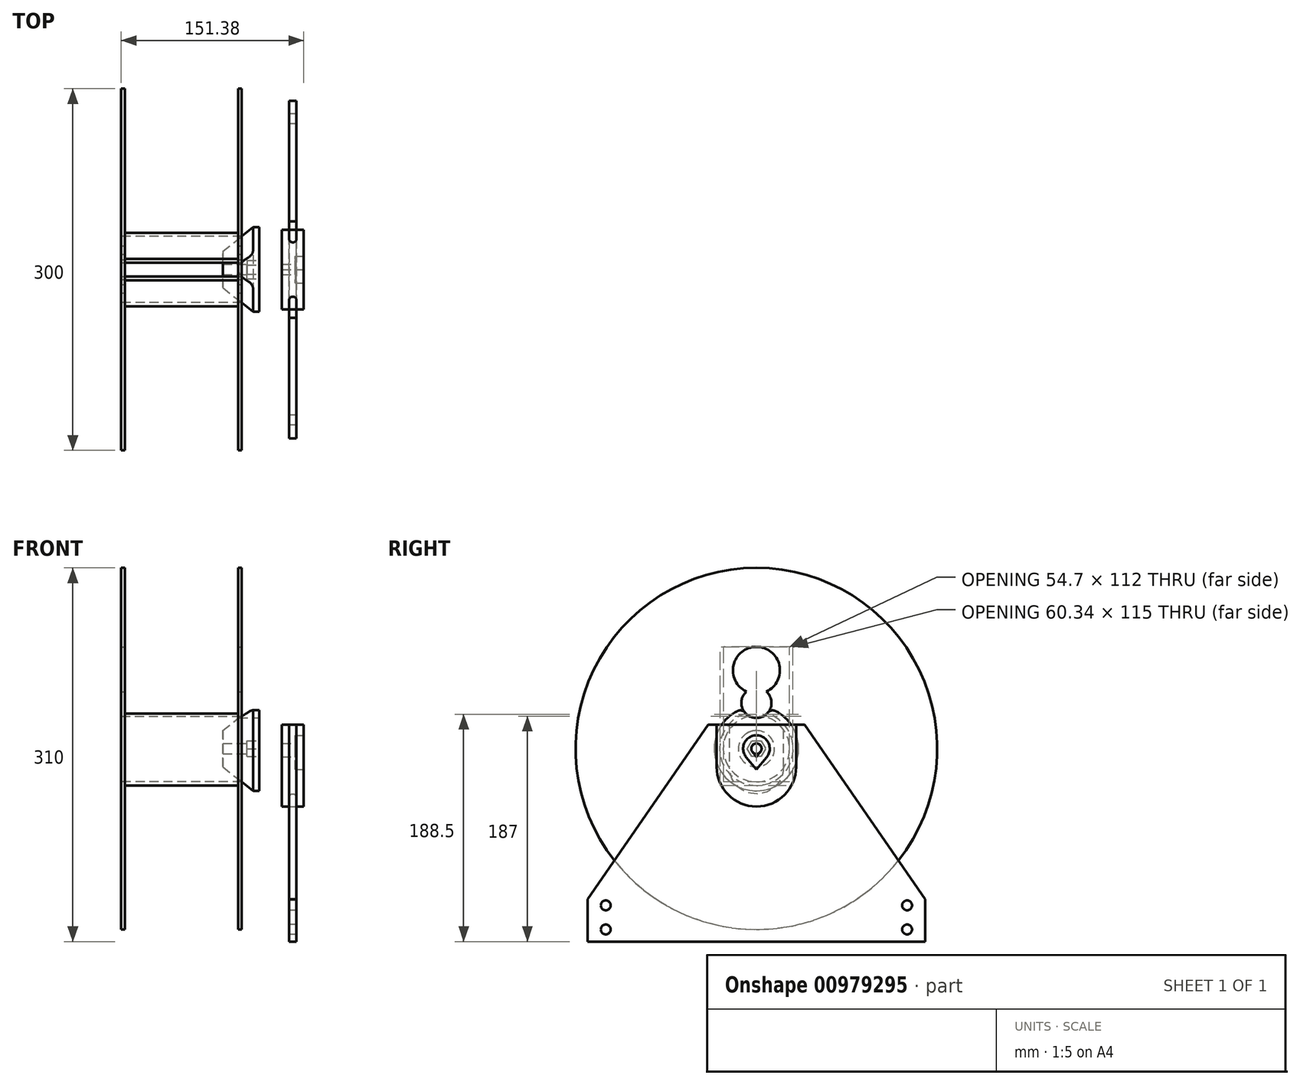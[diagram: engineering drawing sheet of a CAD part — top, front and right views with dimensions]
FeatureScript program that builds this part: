
annotation { "Feature Type Name" : "Feature", "Feature Type Description" : "" }
export const myFeature = defineFeature(function(context is Context, id is Id, definition is map)
    precondition{}
    {
        {
            var Q0;
            Q0=qCreatedBy(makeId("Front.planeOp"),FACE);
            var sketch = newSketch(context, id + "F0", { "sketchPlane" : qUnion([Q0])});
            skLineSegment(sketch, "E0", {"start": v(-50, 150) * mm, "end": v(-50, 27.5) * mm});
            skLineSegment(sketch, "E1", {"start": v(-50, 27.5) * mm, "end": v(50, 27.5) * mm});
            skLineSegment(sketch, "E2", {"start": v(50, 27.5) * mm, "end": v(50, 150) * mm});
            skLineSegment(sketch, "E3", {"start": v(50, 150) * mm, "end": v(47, 150) * mm});
            skLineSegment(sketch, "E4", {"start": v(47, 150) * mm, "end": v(47, 30.5) * mm});
            skLineSegment(sketch, "E5", {"start": v(47, 30.5) * mm, "end": v(-47, 30.5) * mm});
            skLineSegment(sketch, "E6", {"start": v(-47, 30.5) * mm, "end": v(-47, 150) * mm});
            skLineSegment(sketch, "E7", {"start": v(-47, 150) * mm, "end": v(-50, 150) * mm});
            skLineSegment(sketch, "E8", {"start": v(-95.65, 0) * mm, "end": v(81.07, 0) * mm, "construction": true});
            skLineSegment(sketch, "E9", {"start": v(0, 27.5) * mm, "end": v(0, 0) * mm, "construction": true});
            skSolve(sketch);
        }
        {
            var Q0;
            Q0=makeQuery(id+"F0.imprint","IMPRINT",FACE,{"disambiguationData":[TD([[makeQuery(id+"F0.imprint","IMPRINT",EDGE,{"derivedFrom":sQuery(id+"F0.wireOp",EDGE,"E0")}),1.0]])]});
            var Q1;
            Q1=sQuery(id+"F0.wireOp",EDGE,"E8");
            revolve(context, id + "F1", {"surfaceOperationType" : NewSurfaceOperationType.NEW, "entities" : qUnion([Q0]), "axis" : qUnion([Q1]), "revolveType" : RevolveType.FULL});
        }
        {
            var Q0;
            Q0=makeQuery(id+"F1.opRevolve","SWEPT_FACE",FACE,{"disambiguationData":[OSD([sQuery(id+"F0.wireOp",EDGE,"E2")])]});
            var sketch = newSketch(context, id + "F2", { "sketchPlane" : qUnion([Q0])});
            skCircle(sketch, "E10", {"center": v(0, 65) * mm, "radius": 19.5 * mm});
            skSolve(sketch);
        }
        {
            var Q0;
            Q0=makeQuery(id+"F2.imprint","IMPRINT",FACE,{"disambiguationData":[TD([[makeQuery(id+"F2.imprint","IMPRINT",EDGE,{"derivedFrom":sQuery(id+"F2.wireOp",EDGE,"E10")}),1.0]])]});
            extrude(context, id + "F3", {"entities" : qUnion([Q0]), "operationType" : NewBodyOperationType.REMOVE, "endBound" : BoundingType.THROUGH_ALL, "oppositeDirection" : true, "depth" : 25 * mm, "offsetDistance" : 25 * mm});
        }
        {
            var Q0;
            Q0=qCreatedBy(makeId("Front.planeOp"),FACE);
            var sketch = newSketch(context, id + "F4", { "sketchPlane" : qUnion([Q0])});
            skLineSegment(sketch, "E11", {"start": v(12.06, 0) * mm, "end": v(93.62, 0) * mm, "construction": true});
            skLineSegment(sketch, "E12", {"start": v(-35, 27.5) * mm, "end": v(50, 27.5) * mm, "construction": true});
            skLineSegment(sketch, "E13", {"start": v(35, -27.5) * mm, "end": v(-35, -27.5) * mm, "construction": true});
            skLineSegment(sketch, "E14", {"start": v(34.37, 4.1) * mm, "end": v(64.37, 4.1) * mm});
            skLineSegment(sketch, "E15", {"start": v(64.37, 4.1) * mm, "end": v(64.37, 35) * mm});
            skLineSegment(sketch, "E16", {"start": v(64.37, 35) * mm, "end": v(59.37, 35) * mm});
            skLineSegment(sketch, "E17", {"start": v(59.37, 35) * mm, "end": v(34.37, 15) * mm});
            skLineSegment(sketch, "E18", {"start": v(34.37, 15) * mm, "end": v(34.37, 4.1) * mm});
            skSolve(sketch);
        }
        {
            var Q0;
            Q0=qSketchRegion(id+"F4",true);
            var Q1;
            Q1=sQuery(id+"F4.wireOp",EDGE,"E11");
            revolve(context, id + "F5", {"surfaceOperationType" : NewSurfaceOperationType.NEW, "entities" : qUnion([Q0]), "axis" : qUnion([Q1]), "revolveType" : RevolveType.FULL});
        }
        {
            var Q0;
            Q0=makeQuery(id+"F5.opRevolve","SWEPT_FACE",FACE,{"disambiguationData":[OSD([sQuery(id+"F4.wireOp",EDGE,"E15")])]});
            var sketch = newSketch(context, id + "F6", { "sketchPlane" : qUnion([Q0])});
            skCircle(sketch, "E19", {"center": v(0, 38) * mm, "radius": 12.5 * mm});
            skSolve(sketch);
        }
        {
            var Q0;
            Q0=qSketchRegion(id+"F6",true);
            extrude(context, id + "F7", {"entities" : qUnion([Q0]), "operationType" : NewBodyOperationType.REMOVE, "endBound" : BoundingType.THROUGH_ALL, "oppositeDirection" : true, "depth" : 25 * mm, "offsetDistance" : 25 * mm});
        }
        {
            var Q0;
            Q0=makeQuery(id+"F7.boolean.opBoolean","INTERSECT",EDGE,{"disambiguationData":[OD(1.0)],"derivedFrom":[makeQuery(id+"F5.opRevolve","SWEPT_FACE",FACE,{"disambiguationData":[OSD([sQuery(id+"F4.wireOp",EDGE,"E16")])]}),makeQuery(id+"F7.opExtrude","SWEPT_FACE",FACE,{"disambiguationData":[OSD([sQuery(id+"F6.wireOp",EDGE,"E19")])]})]});
            var Q1;
            Q1=makeQuery(id+"F7.boolean.opBoolean","INTERSECT",EDGE,{"disambiguationData":[OD(0.0)],"derivedFrom":[makeQuery(id+"F5.opRevolve","SWEPT_FACE",FACE,{"disambiguationData":[OSD([sQuery(id+"F4.wireOp",EDGE,"E16")])]}),makeQuery(id+"F7.opExtrude","SWEPT_FACE",FACE,{"disambiguationData":[OSD([sQuery(id+"F6.wireOp",EDGE,"E19")])]})]});
            fillet(context, id + "F8", {"entities" : qUnion([Q0, Q1]), "radius" : 5 * mm, "tangentPropagation" : true, "allowEdgeOverflow" : false});
        }
        {
            var Q0;
            Q0=makeQuery(id+"F5.opRevolve","SWEPT_FACE",FACE,{"disambiguationData":[OSD([sQuery(id+"F4.wireOp",EDGE,"E15")])]});
            var sketch = newSketch(context, id + "F9", { "sketchPlane" : qUnion([Q0])});
            skCircle(sketch, "E20.cCircle", {"center": v(0, 0) * mm, "radius": 6.55 * mm, "construction": true});
            skLineSegment(sketch, "E20.0", {"start": v(-3.78, 6.55) * mm, "end": v(3.78, 6.55) * mm});
            skLineSegment(sketch, "E20.1", {"start": v(3.78, 6.55) * mm, "end": v(7.56, 0) * mm});
            skLineSegment(sketch, "E20.2", {"start": v(7.56, 0) * mm, "end": v(3.78, -6.55) * mm});
            skLineSegment(sketch, "E20.3", {"start": v(3.78, -6.55) * mm, "end": v(-3.78, -6.55) * mm});
            skLineSegment(sketch, "E20.4", {"start": v(-3.78, -6.55) * mm, "end": v(-7.56, 0) * mm});
            skLineSegment(sketch, "E20.5", {"start": v(-7.56, 0) * mm, "end": v(-3.78, 6.55) * mm});
            skPoint(sketch, "E20.0.midPoint", {"position": v(0, 6.55) * mm});
            skSolve(sketch);
        }
        {
            var Q0;
            Q0=qSketchRegion(id+"F9",true);
            extrude(context, id + "F10", {"entities" : qUnion([Q0]), "operationType" : NewBodyOperationType.REMOVE, "oppositeDirection" : true, "depth" : 10 * mm, "offsetDistance" : 25 * mm});
        }
        {
            var Q0;
            Q0=makeQuery(id+"F5.opRevolve","SWEPT_BODY",BODY,{"disambiguationData":[OSD([sQuery(id+"F4.wireOp",EDGE,"E14"),sQuery(id+"F4.wireOp",EDGE,"E15"),sQuery(id+"F4.wireOp",EDGE,"E16"),sQuery(id+"F4.wireOp",EDGE,"E17"),sQuery(id+"F4.wireOp",EDGE,"E18")])]});
            transform(context, id + "F11", {"entities" : qUnion([Q0]), "transformType" : TransformType.TRANSLATION_3D, "dx" : 0 * mm, "dy" : 0 * mm, "dz" : 0 * mm, "makeCopy" : true});
        }
        {
            var Q0;
            Q0=makeQuery(id+"F11.opPattern","COPY",BODY,{"derivedFrom":makeQuery(id+"F5.opRevolve","SWEPT_BODY",BODY,{"disambiguationData":[OSD([sQuery(id+"F4.wireOp",EDGE,"E14"),sQuery(id+"F4.wireOp",EDGE,"E15"),sQuery(id+"F4.wireOp",EDGE,"E16"),sQuery(id+"F4.wireOp",EDGE,"E17"),sQuery(id+"F4.wireOp",EDGE,"E18")])]}),"instanceName":"1"});
            deleteBodies(context, id + "F12", {"entities" : qUnion([Q0])});
        }
        {
            var Q0;
            Q0=makeQuery(id+"F5.opRevolve","SWEPT_FACE",FACE,{"disambiguationData":[OSD([sQuery(id+"F4.wireOp",EDGE,"E15")])]});
            cPlane(context, id + "F13", {"entities" : qUnion([Q0]), "cplaneType" : CPlaneType.OFFSET, "offset" : 25 * mm, "width" : 150 * mm, "height" : 150 * mm});
        }
        {
            var Q0;
            Q0=qCreatedBy(id+"F13.planeOp",FACE);
            var sketch = newSketch(context, id + "F14", { "sketchPlane" : qUnion([Q0])});
            skLineSegment(sketch, "E21", {"start": v(-140, -160) * mm, "end": v(-140, -125) * mm});
            skLineSegment(sketch, "E22", {"start": v(-140, -125) * mm, "end": v(-40, 20) * mm});
            skLineSegment(sketch, "E23", {"start": v(-40, 20) * mm, "end": v(-25, 20) * mm});
            skLineSegment(sketch, "E24", {"start": v(-25, 20) * mm, "end": v(-25, -15) * mm});
            skLineSegment(sketch, "E25", {"start": v(-25, -15) * mm, "end": v(25, -15) * mm, "construction": true});
            skLineSegment(sketch, "E26", {"start": v(25, -15) * mm, "end": v(25, 20) * mm});
            skLineSegment(sketch, "E27", {"start": v(25, 20) * mm, "end": v(40, 20) * mm});
            skLineSegment(sketch, "E28", {"start": v(40, 20) * mm, "end": v(140, -125) * mm});
            skLineSegment(sketch, "E29", {"start": v(140, -125) * mm, "end": v(140, -160) * mm});
            skLineSegment(sketch, "E30", {"start": v(140, -160) * mm, "end": v(-140, -160) * mm});
            skLineSegment(sketch, "E31", {"start": v(0, -160) * mm, "end": v(0, 0) * mm, "construction": true});
            skArc(sketch, "E32", {"start": v(-25, -15) * mm, "mid": v(0, -40) * mm, "end": v(25, -15) * mm});
            skCircle(sketch, "E33", {"center": v(-125, -130) * mm, "radius": 4.1 * mm});
            skCircle(sketch, "E34", {"center": v(-125, -150) * mm, "radius": 4.1 * mm});
            skCircle(sketch, "E35", {"center": v(125, -130) * mm, "radius": 4.1 * mm});
            skCircle(sketch, "E36", {"center": v(125, -150) * mm, "radius": 4.1 * mm});
            skLineSegment(sketch, "E37", {"start": v(-125, -130) * mm, "end": v(125, -130) * mm, "construction": true});
            skLineSegment(sketch, "E38", {"start": v(125, -130) * mm, "end": v(125, -150) * mm, "construction": true});
            skLineSegment(sketch, "E39", {"start": v(125, -150) * mm, "end": v(-125, -150) * mm, "construction": true});
            skLineSegment(sketch, "E40", {"start": v(-125, -150) * mm, "end": v(-125, -130) * mm, "construction": true});
            skSolve(sketch);
        }
        {
            var Q0;
            Q0=makeQuery(id+"F14.imprint","IMPRINT",FACE,{"disambiguationData":[TD([[makeQuery(id+"F14.imprint","IMPRINT",EDGE,{"derivedFrom":sQuery(id+"F14.wireOp",EDGE,"E21")}),-1.0]])]});
            extrude(context, id + "F15", {"entities" : qUnion([Q0]), "depth" : 6 * mm, "offsetDistance" : 25 * mm});
        }
        {
            var Q0;
            Q0=makeQuery(id+"F15.opExtrude","CAP_FACE",FACE,{"disambiguationData":[OSD([sQuery(id+"F14.wireOp",EDGE,"E21"),sQuery(id+"F14.wireOp",EDGE,"E22"),sQuery(id+"F14.wireOp",EDGE,"E23"),sQuery(id+"F14.wireOp",EDGE,"E24"),sQuery(id+"F14.wireOp",EDGE,"E26"),sQuery(id+"F14.wireOp",EDGE,"E27"),sQuery(id+"F14.wireOp",EDGE,"E28"),sQuery(id+"F14.wireOp",EDGE,"E29"),sQuery(id+"F14.wireOp",EDGE,"E30"),sQuery(id+"F14.wireOp",EDGE,"E32"),sQuery(id+"F14.wireOp",EDGE,"E33"),sQuery(id+"F14.wireOp",EDGE,"E34"),sQuery(id+"F14.wireOp",EDGE,"E35"),sQuery(id+"F14.wireOp",EDGE,"E36")])],"isStart":false});
            cPlane(context, id + "F16", {"entities" : qUnion([Q0]), "cplaneType" : CPlaneType.OFFSET, "offset" : 3 * mm, "oppositeDirection" : true, "width" : 150 * mm, "height" : 150 * mm});
        }
        {
            var Q0;
            Q0=qCreatedBy(id+"F16.planeOp",FACE);
            var sketch = newSketch(context, id + "F17", { "sketchPlane" : qUnion([Q0])});
            skLineSegment(sketch, "E41.0", {"start": v(-25, 20) * mm, "end": v(-25, -15) * mm});
            skArc(sketch, "E42.0", {"start": v(-25, -15) * mm, "mid": v(0, -40) * mm, "end": v(25, -15) * mm});
            skLineSegment(sketch, "E43.0", {"start": v(25, -15) * mm, "end": v(25, 20) * mm});
            skLineSegment(sketch, "E44.0", {"start": v(33, -15) * mm, "end": v(33, 20) * mm});
            skArc(sketch, "E44.1", {"start": v(-33, -15) * mm, "mid": v(0, -48) * mm, "end": v(33, -15) * mm});
            skLineSegment(sketch, "E44.2", {"start": v(-33, 20) * mm, "end": v(-33, -15) * mm});
            skLineSegment(sketch, "E45", {"start": v(-33, 20) * mm, "end": v(33, 20) * mm});
            skSolve(sketch);
        }
        {
            var Q0;
            {var subQ2=sQuery(id+"F17.wireOp",EDGE,"E41.0");Q0=makeQuery(id+"F17.imprint","IMPRINT",FACE,{"disambiguationData":[TD([[makeQuery(id+"F17.imprint","IMPRINT",EDGE,{"derivedFrom":subQ2}),-1.0]])]});}
            var Q1;
            {var subQ0=sQuery(id+"F17.wireOp",EDGE,"E41.0");Q1=makeQuery(id+"F17.imprint","IMPRINT",FACE,{"disambiguationData":[TD([[makeQuery(id+"F17.imprint","IMPRINT",EDGE,{"derivedFrom":subQ0}),1.0]])]});}
            extrude(context, id + "F18", {"entities" : qUnion([Q0, Q1]), "endBound" : BoundingType.SYMMETRIC, "depth" : 18 * mm, "offsetDistance" : 25 * mm});
        }
        {
            var Q0;
            Q0=makeQuery(id+"F18.opExtrude","SWEPT_FACE",FACE,{"disambiguationData":[OSD([sQuery(id+"F17.wireOp",EDGE,"E45")])]});
            var sketch = newSketch(context, id + "F19", { "sketchPlane" : qUnion([Q0])});
            skLineSegment(sketch, "E46", {"start": v(89.27, -33) * mm, "end": v(89.27, -25.6) * mm});
            skLineSegment(sketch, "E47", {"start": v(89.27, -25.6) * mm, "end": v(95.48, -25.6) * mm, "construction": true});
            skLineSegment(sketch, "E48", {"start": v(95.47, -25.6) * mm, "end": v(95.47, -33) * mm});
            skLineSegment(sketch, "E49", {"start": v(95.48, -33) * mm, "end": v(89.27, -33) * mm});
            skArc(sketch, "E50", {"start": v(89.28, -25.6) * mm, "mid": v(92.38, -22.5) * mm, "end": v(95.47, -25.6) * mm});
            skSolve(sketch);
        }
        {
            var Q0;
            Q0=makeQuery(id+"F19.imprint","IMPRINT",FACE,{"disambiguationData":[TD([[makeQuery(id+"F19.imprint","IMPRINT",EDGE,{"derivedFrom":sQuery(id+"F19.wireOp",EDGE,"E46")}),-1.0]])]});
            var Q1;
            Q1=makeQuery(id+"F18.opExtrude","CAP_EDGE",EDGE,{"disambiguationData":[OSD([sQuery(id+"F17.wireOp",EDGE,"E44.2")])],"isStart":false});
            var Q2;
            Q2=makeQuery(id+"F18.opExtrude","CAP_EDGE",EDGE,{"disambiguationData":[OSD([sQuery(id+"F17.wireOp",EDGE,"E44.1")])],"isStart":false});
            var Q3;
            Q3=makeQuery(id+"F18.opExtrude","CAP_EDGE",EDGE,{"disambiguationData":[OSD([sQuery(id+"F17.wireOp",EDGE,"E44.0")])],"isStart":false});
            sweep(context, id + "F20", {"operationType" : NewBodyOperationType.REMOVE, "profiles" : qUnion([Q0]), "path" : qUnion([Q1, Q2, Q3])});
        }
        {
            var Q0;
            Q0=makeQuery(id+"F18.opExtrude","CAP_FACE",FACE,{"disambiguationData":[OSD([sQuery(id+"F17.wireOp",EDGE,"E44.0"),sQuery(id+"F17.wireOp",EDGE,"E44.1"),sQuery(id+"F17.wireOp",EDGE,"E44.2"),sQuery(id+"F17.wireOp",EDGE,"E45")])],"isStart":false});
            var sketch = newSketch(context, id + "F21", { "sketchPlane" : qUnion([Q0])});
            skCircle(sketch, "E51.0", {"center": v(0, 0) * mm, "radius": 4.1 * mm});
            skCircle(sketch, "E52", {"center": v(0, 0) * mm, "radius": 11.05 * mm});
            skCircle(sketch, "E53.0", {"center": v(0, 0) * mm, "radius": 4.3 * mm});
            skSolve(sketch);
        }
        {
            var Q0;
            Q0=makeQuery(id+"F21.imprint","IMPRINT",FACE,{"disambiguationData":[TD([[makeQuery(id+"F21.imprint","IMPRINT",EDGE,{"derivedFrom":sQuery(id+"F21.wireOp",EDGE,"E52")}),1.0]])]});
            var Q1;
            Q1=makeQuery(id+"F21.imprint","IMPRINT",FACE,{"disambiguationData":[TD([[makeQuery(id+"F21.imprint","IMPRINT",EDGE,{"derivedFrom":sQuery(id+"F21.wireOp",EDGE,"E51.0")}),1.0]])]});
            var Q2;
            Q2=makeQuery(id+"F21.imprint","IMPRINT",FACE,{"disambiguationData":[TD([[makeQuery(id+"F21.imprint","IMPRINT",EDGE,{"derivedFrom":sQuery(id+"F21.wireOp",EDGE,"E51.0")}),-1.0]])]});
            extrude(context, id + "F22", {"entities" : qUnion([Q0, Q1, Q2]), "operationType" : NewBodyOperationType.REMOVE, "oppositeDirection" : true, "depth" : 7 * mm, "offsetDistance" : 25 * mm});
        }
        {
            var Q0;
            Q0=makeQuery(id+"F21.imprint","IMPRINT",FACE,{"disambiguationData":[TD([[makeQuery(id+"F21.imprint","IMPRINT",EDGE,{"derivedFrom":sQuery(id+"F21.wireOp",EDGE,"E51.0")}),1.0]])]});
            var Q1;
            Q1=makeQuery(id+"F21.imprint","IMPRINT",FACE,{"disambiguationData":[TD([[makeQuery(id+"F21.imprint","IMPRINT",EDGE,{"derivedFrom":sQuery(id+"F21.wireOp",EDGE,"E51.0")}),-1.0]])]});
            extrude(context, id + "F23", {"entities" : qUnion([Q0, Q1]), "operationType" : NewBodyOperationType.REMOVE, "endBound" : BoundingType.THROUGH_ALL, "oppositeDirection" : true, "depth" : 25 * mm, "offsetDistance" : 25 * mm});
        }
        {
            var Q0;
            Q0=makeQuery(id+"F18.opExtrude","CAP_FACE",FACE,{"disambiguationData":[OSD([sQuery(id+"F17.wireOp",EDGE,"E44.0"),sQuery(id+"F17.wireOp",EDGE,"E44.1"),sQuery(id+"F17.wireOp",EDGE,"E44.2"),sQuery(id+"F17.wireOp",EDGE,"E45")])],"isStart":false});
            var sketch = newSketch(context, id + "F24", { "sketchPlane" : qUnion([Q0])});
            skLineSegment(sketch, "E54", {"start": v(0, 0) * mm, "end": v(0, -29.5) * mm, "construction": true});
            skLineSegment(sketch, "E55", {"start": v(-8.46, -7.1) * mm, "end": v(0, -17.2) * mm});
            skLineSegment(sketch, "E56.MirrorCS", {"start": v(8.46, -7.1) * mm, "end": v(0, -17.2) * mm});
            skSolve(sketch);
        }
        {
            var Q0;
            {var subQ0=sQuery(id+"F24.wireOp",EDGE,"E55");Q0=makeQuery(id+"F24.imprint","IMPRINT",FACE,{"disambiguationData":[TD([[makeQuery(id+"F24.imprint","IMPRINT",EDGE,{"derivedFrom":subQ0}),1.0]])]});}
            var Q1;
            Q1=makeQuery(id+"F22.boolean.opBoolean","COPY",FACE,{"derivedFrom":makeQuery(id+"F22.opExtrude","CAP_FACE",FACE,{"disambiguationData":[OSD([sQuery(id+"F21.wireOp",EDGE,"E52")])],"isStart":false})});
            extrude(context, id + "F25", {"entities" : qUnion([Q0]), "operationType" : NewBodyOperationType.REMOVE, "endBound" : BoundingType.UP_TO_SURFACE, "oppositeDirection" : true, "depth" : 25 * mm, "endBoundEntityFace" : qUnion([Q1]), "offsetDistance" : 25 * mm});
        }
        {
            var Q0;
            {var subQ0=sQuery(id+"F21.wireOp",EDGE,"E52");Q0=makeQuery(id+"F25.boolean.opBoolean","MERGE",FACE,{"derivedFrom":[makeQuery(id+"F22.boolean.opBoolean","COPY",FACE,{"derivedFrom":makeQuery(id+"F22.opExtrude","CAP_FACE",FACE,{"disambiguationData":[OSD([subQ0])],"isStart":false})})],"fromTools":[makeQuery(id+"F25.opExtrude","CAP_FACE",FACE,{"disambiguationData":[OSD([subQ0,sQuery(id+"F24.wireOp",EDGE,"E55"),sQuery(id+"F24.wireOp",EDGE,"E56.MirrorCS")])],"isStart":false})]});}
            var sketch = newSketch(context, id + "F26", { "sketchPlane" : qUnion([Q0])});
            skLineSegment(sketch, "E57", {"start": v(0, 0) * mm, "end": v(0, -10.4) * mm, "construction": true});
            skLineSegment(sketch, "E58", {"start": v(-3.3, -2.76) * mm, "end": v(0, -6.69) * mm});
            skLineSegment(sketch, "E59.MirrorCS", {"start": v(3.3, -2.76) * mm, "end": v(0, -6.69) * mm});
            skSolve(sketch);
        }
        {
            var Q0;
            {var subQ0=sQuery(id+"F26.wireOp",EDGE,"E58");Q0=makeQuery(id+"F26.imprint","IMPRINT",FACE,{"disambiguationData":[TD([[makeQuery(id+"F26.imprint","IMPRINT",EDGE,{"derivedFrom":subQ0}),1.0]])]});}
            extrude(context, id + "F27", {"entities" : qUnion([Q0]), "operationType" : NewBodyOperationType.REMOVE, "endBound" : BoundingType.UP_TO_NEXT, "oppositeDirection" : true, "depth" : 25 * mm, "offsetDistance" : 25 * mm});
        }
    });
